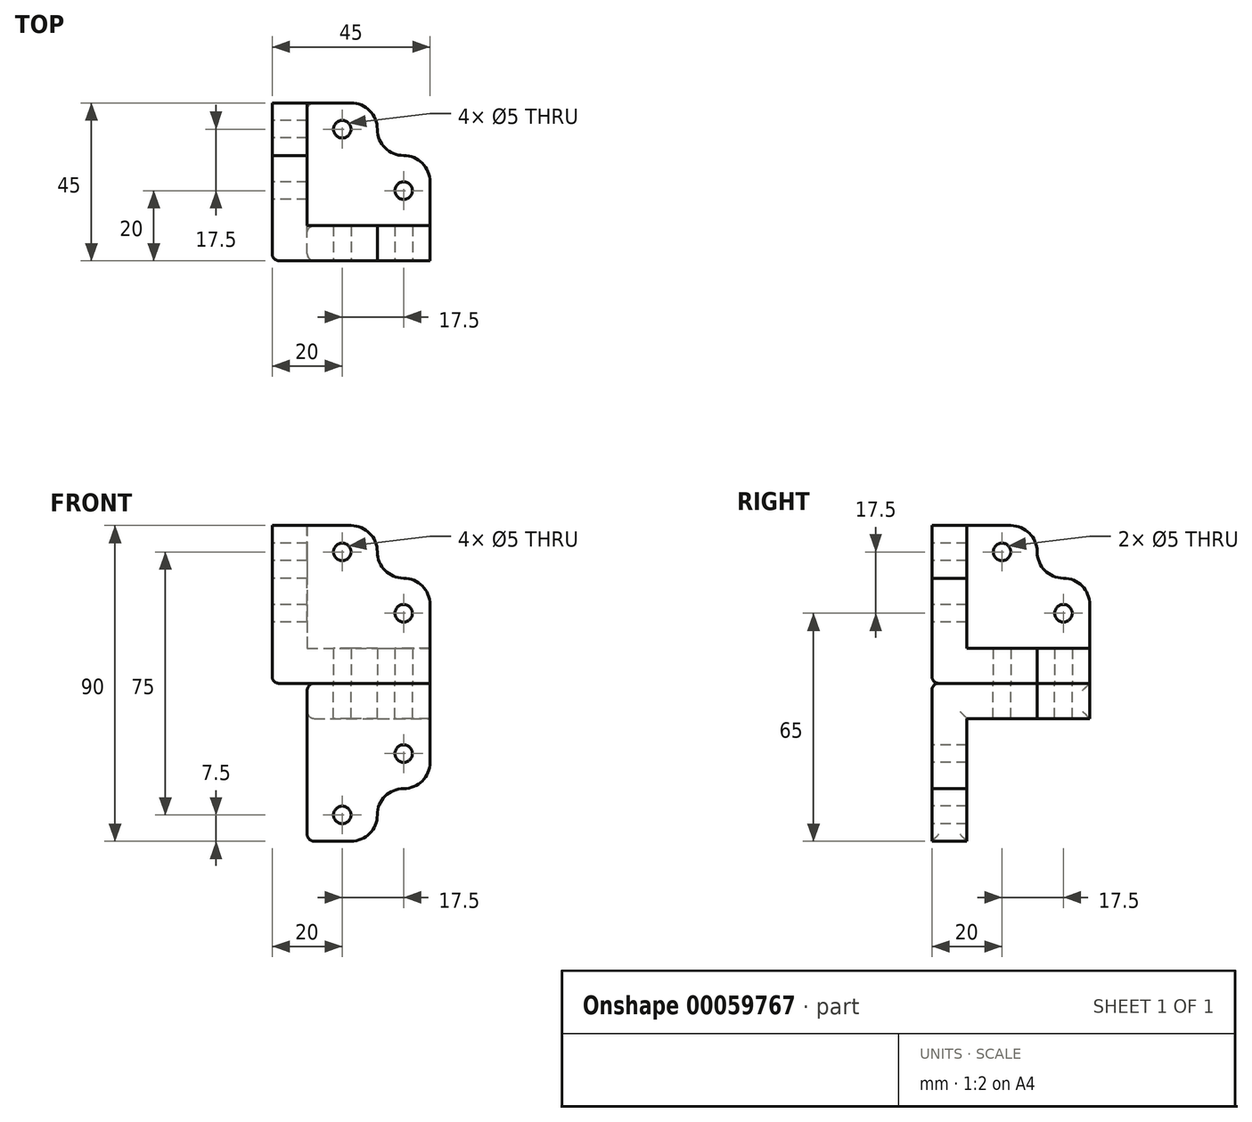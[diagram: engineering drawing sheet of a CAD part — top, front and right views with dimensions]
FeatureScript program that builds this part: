
annotation { "Feature Type Name" : "Feature", "Feature Type Description" : "" }
export const myFeature = defineFeature(function(context is Context, id is Id, definition is map)
    precondition{}
    {
        {
            var Q0;
            Q0=qCreatedBy(makeId("Top.planeOp"),FACE);
            var sketch = newSketch(context, id + "F0", { "sketchPlane" : qUnion([Q0])});
            skLineSegment(sketch, "E0", {"start": v(10, 45) * mm, "end": v(10, 10) * mm});
            skLineSegment(sketch, "E1", {"start": v(10, 10) * mm, "end": v(45, 10) * mm});
            skLineSegment(sketch, "E2", {"start": v(45, 10) * mm, "end": v(45, 30) * mm});
            skLineSegment(sketch, "E3", {"start": v(45, 30) * mm, "end": v(30, 30) * mm});
            skLineSegment(sketch, "E4", {"start": v(30, 30) * mm, "end": v(30, 45) * mm});
            skLineSegment(sketch, "E5", {"start": v(30, 45) * mm, "end": v(10, 45) * mm});
            skLineSegment(sketch, "E6", {"start": v(45, 10) * mm, "end": v(45, 0) * mm});
            skLineSegment(sketch, "E7", {"start": v(45, 0) * mm, "end": v(0, 0) * mm});
            skLineSegment(sketch, "E8", {"start": v(0, 0) * mm, "end": v(0, 45) * mm});
            skLineSegment(sketch, "E9", {"start": v(0, 45) * mm, "end": v(10, 45) * mm});
            skCircle(sketch, "E10", {"center": v(20, 37.5) * mm, "radius": 2.5 * mm});
            skPoint(sketch, "E10.centerSnap0", {"position": v(30, 37.5) * mm});
            skPoint(sketch, "E10.centerSnap1", {"position": v(20, 45) * mm});
            skCircle(sketch, "E11", {"center": v(37.5, 20) * mm, "radius": 2.5 * mm});
            skPoint(sketch, "E11.centerSnap0", {"position": v(45, 20) * mm});
            skPoint(sketch, "E11.centerSnap1", {"position": v(37.5, 30) * mm});
            skPoint(sketch, "E12.0", {"position": v(0, 0) * mm});
            skSolve(sketch);
        }
        {
            var Q0;
            Q0=makeQuery(id+"F0.imprint","IMPRINT",FACE,{"disambiguationData":[TD([[makeQuery(id+"F0.imprint","IMPRINT",EDGE,{"derivedFrom":sQuery(id+"F0.wireOp",EDGE,"E0")}),-1.0]])]});
            var Q1;
            Q1=makeQuery(id+"F0.imprint","IMPRINT",FACE,{"disambiguationData":[TD([[makeQuery(id+"F0.imprint","IMPRINT",EDGE,{"derivedFrom":sQuery(id+"F0.wireOp",EDGE,"E0")}),1.0]])]});
            extrude(context, id + "F1", {"entities" : qUnion([Q0, Q1]), "depth" : 10 * mm});
        }
        {
            var Q0;
            Q0=qCreatedBy(makeId("Right.planeOp"),FACE);
            var sketch = newSketch(context, id + "F2", { "sketchPlane" : qUnion([Q0])});
            skLineSegment(sketch, "E13", {"start": v(10, 45) * mm, "end": v(10, 10) * mm});
            skLineSegment(sketch, "E14", {"start": v(10, 10) * mm, "end": v(45, 10) * mm});
            skLineSegment(sketch, "E15", {"start": v(45, 10) * mm, "end": v(45, 30) * mm});
            skLineSegment(sketch, "E16", {"start": v(45, 30) * mm, "end": v(30, 30) * mm});
            skLineSegment(sketch, "E17", {"start": v(30, 30) * mm, "end": v(30, 45) * mm});
            skLineSegment(sketch, "E18", {"start": v(30, 45) * mm, "end": v(10, 45) * mm});
            skLineSegment(sketch, "E19", {"start": v(45, 10) * mm, "end": v(45, 0) * mm});
            skLineSegment(sketch, "E20", {"start": v(45, 0) * mm, "end": v(0, 0) * mm});
            skLineSegment(sketch, "E21", {"start": v(0, 0) * mm, "end": v(0, 45) * mm});
            skLineSegment(sketch, "E22", {"start": v(0, 45) * mm, "end": v(10, 45) * mm});
            skCircle(sketch, "E23", {"center": v(20, 37.5) * mm, "radius": 2.5 * mm});
            skPoint(sketch, "E23.centerSnap0", {"position": v(30, 37.5) * mm});
            skPoint(sketch, "E23.centerSnap1", {"position": v(20, 45) * mm});
            skCircle(sketch, "E24", {"center": v(37.5, 20) * mm, "radius": 2.5 * mm});
            skPoint(sketch, "E24.centerSnap0", {"position": v(45, 20) * mm});
            skPoint(sketch, "E24.centerSnap1", {"position": v(37.5, 30) * mm});
            skPoint(sketch, "E25", {"position": v(0, 0) * mm});
            skSolve(sketch);
        }
        {
            var Q0;
            Q0=makeQuery(id+"F2.imprint","IMPRINT",FACE,{"disambiguationData":[TD([[makeQuery(id+"F2.imprint","IMPRINT",EDGE,{"derivedFrom":sQuery(id+"F2.wireOp",EDGE,"2a13ad23-5e3c-4e8f-b476-5bc90f6551fb")}),1.0]])]});
            var Q1;
            Q1=makeQuery(id+"F2.imprint","IMPRINT",FACE,{"disambiguationData":[TD([[makeQuery(id+"F2.imprint","IMPRINT",EDGE,{"derivedFrom":sQuery(id+"F2.wireOp",EDGE,"2a13ad23-5e3c-4e8f-b476-5bc90f6551fb")}),-1.0]])]});
            var Q2;
            Q2=makeQuery(id+"F2.imprint","IMPRINT",FACE,{"disambiguationData":[TD([[makeQuery(id+"F2.imprint","IMPRINT",EDGE,{"derivedFrom":sQuery(id+"F2.wireOp",EDGE,"E13")}),-1.0]])]});
            var Q3;
            Q3=makeQuery(id+"F2.imprint","IMPRINT",FACE,{"disambiguationData":[TD([[makeQuery(id+"F2.imprint","IMPRINT",EDGE,{"derivedFrom":sQuery(id+"F2.wireOp",EDGE,"E13")}),1.0]])]});
            extrude(context, id + "F3", {"entities" : qUnion([Q0, Q1, Q2, Q3]), "operationType" : NewBodyOperationType.ADD, "depth" : 10 * mm});
        }
        {
            var Q0;
            Q0=qCreatedBy(makeId("Front.planeOp"),FACE);
            var sketch = newSketch(context, id + "F4", { "sketchPlane" : qUnion([Q0])});
            skPoint(sketch, "E26", {"position": v(0, 0) * mm});
            skLineSegment(sketch, "E27", {"start": v(10, 45) * mm, "end": v(10, 10) * mm});
            skLineSegment(sketch, "E28", {"start": v(10, 10) * mm, "end": v(45, 10) * mm});
            skLineSegment(sketch, "E29", {"start": v(45, 10) * mm, "end": v(45, 30) * mm});
            skLineSegment(sketch, "E30", {"start": v(45, 30) * mm, "end": v(30, 30) * mm});
            skLineSegment(sketch, "E31", {"start": v(30, 30) * mm, "end": v(30, 45) * mm});
            skLineSegment(sketch, "E32", {"start": v(30, 45) * mm, "end": v(10, 45) * mm});
            skLineSegment(sketch, "E33", {"start": v(45, 10) * mm, "end": v(45, 0) * mm});
            skLineSegment(sketch, "E34", {"start": v(45, 0) * mm, "end": v(0, 0) * mm});
            skLineSegment(sketch, "E35", {"start": v(0, 0) * mm, "end": v(0, 45) * mm});
            skLineSegment(sketch, "E36", {"start": v(0, 45) * mm, "end": v(10, 45) * mm});
            skCircle(sketch, "E37", {"center": v(20, 37.5) * mm, "radius": 2.5 * mm});
            skPoint(sketch, "E37.centerSnap0", {"position": v(30, 37.5) * mm});
            skPoint(sketch, "E37.centerSnap1", {"position": v(20, 45) * mm});
            skCircle(sketch, "E38", {"center": v(37.5, 20) * mm, "radius": 2.5 * mm});
            skPoint(sketch, "E38.centerSnap0", {"position": v(45, 20) * mm});
            skPoint(sketch, "E38.centerSnap1", {"position": v(37.5, 30) * mm});
            skSolve(sketch);
        }
        {
            var Q0;
            Q0=makeQuery(id+"F4.imprint","IMPRINT",FACE,{"disambiguationData":[TD([[makeQuery(id+"F4.imprint","IMPRINT",EDGE,{"derivedFrom":sQuery(id+"F4.wireOp",EDGE,"64c80488-47ea-4c83-bcab-fc076bb4a540")}),-1.0]])]});
            var Q1;
            Q1=makeQuery(id+"F4.imprint","IMPRINT",FACE,{"disambiguationData":[TD([[makeQuery(id+"F4.imprint","IMPRINT",EDGE,{"derivedFrom":sQuery(id+"F4.wireOp",EDGE,"64c80488-47ea-4c83-bcab-fc076bb4a540")}),1.0]])]});
            var Q2;
            Q2=makeQuery(id+"F4.imprint","IMPRINT",FACE,{"disambiguationData":[TD([[makeQuery(id+"F4.imprint","IMPRINT",EDGE,{"derivedFrom":sQuery(id+"F4.wireOp",EDGE,"E27")}),-1.0]])]});
            var Q3;
            Q3=makeQuery(id+"F4.imprint","IMPRINT",FACE,{"disambiguationData":[TD([[makeQuery(id+"F4.imprint","IMPRINT",EDGE,{"derivedFrom":sQuery(id+"F4.wireOp",EDGE,"E27")}),1.0]])]});
            extrude(context, id + "F5", {"entities" : qUnion([Q0, Q1, Q2, Q3]), "operationType" : NewBodyOperationType.ADD, "oppositeDirection" : true, "depth" : 10 * mm});
        }
        {
            var Q0;
            Q0=makeQuery(id+"F1.opExtrude","CAP_EDGE",EDGE,{"disambiguationData":[OSD([sQuery(id+"F0.wireOp",EDGE,"E7")])],"isStart":true});
            var Q1;
            Q1=makeQuery(id+"F3.boolean.opBoolean","MERGE",EDGE,{"derivedFrom":[makeQuery(id+"F1.opExtrude","SWEPT_EDGE",EDGE,{"disambiguationData":[OSD([sQuery(id+"F0.wireOp",EDGE,"E7"),sQuery(id+"F0.wireOp",EDGE,"E8")])]}),makeQuery(id+"F3.opExtrude","CAP_EDGE",EDGE,{"disambiguationData":[OSD([sQuery(id+"F2.wireOp",EDGE,"E21")])],"isStart":true})]});
            var Q2;
            Q2=makeQuery(id+"F1.opExtrude","CAP_EDGE",EDGE,{"disambiguationData":[OSD([sQuery(id+"F0.wireOp",EDGE,"E8")])],"isStart":true});
            fillet(context, id + "F6", {"entities" : qUnion([Q0, Q1, Q2]), "radius" : 2 * mm, "tangentPropagation" : true, "allowEdgeOverflow" : false});
        }
        {
            var Q0;
            Q0=makeQuery(id+"F5.opExtrude","SWEPT_EDGE",EDGE,{"disambiguationData":[OSD([sQuery(id+"F4.wireOp",EDGE,"E29"),sQuery(id+"F4.wireOp",EDGE,"E30")])]});
            var Q1;
            Q1=makeQuery(id+"F5.opExtrude","SWEPT_EDGE",EDGE,{"disambiguationData":[OSD([sQuery(id+"F4.wireOp",EDGE,"E31"),sQuery(id+"F4.wireOp",EDGE,"E32")])]});
            var Q2;
            Q2=makeQuery(id+"F3.opExtrude","SWEPT_EDGE",EDGE,{"disambiguationData":[OSD([sQuery(id+"F2.wireOp",EDGE,"E17"),sQuery(id+"F2.wireOp",EDGE,"E18")])]});
            var Q3;
            Q3=makeQuery(id+"F3.opExtrude","SWEPT_EDGE",EDGE,{"disambiguationData":[OSD([sQuery(id+"F2.wireOp",EDGE,"E15"),sQuery(id+"F2.wireOp",EDGE,"E16")])]});
            var Q4;
            Q4=makeQuery(id+"F1.opExtrude","SWEPT_EDGE",EDGE,{"disambiguationData":[OSD([sQuery(id+"F0.wireOp",EDGE,"E4"),sQuery(id+"F0.wireOp",EDGE,"E5")])]});
            var Q5;
            Q5=makeQuery(id+"F1.opExtrude","SWEPT_EDGE",EDGE,{"disambiguationData":[OSD([sQuery(id+"F0.wireOp",EDGE,"E2"),sQuery(id+"F0.wireOp",EDGE,"E3")])]});
            fillet(context, id + "F7", {"entities" : qUnion([Q0, Q1, Q2, Q3, Q4, Q5]), "radius" : 7.5 * mm, "tangentPropagation" : true, "allowEdgeOverflow" : false});
        }
        {
            var Q0;
            Q0=makeQuery(id+"F5.opExtrude","SWEPT_EDGE",EDGE,{"disambiguationData":[OSD([sQuery(id+"F4.wireOp",EDGE,"E30"),sQuery(id+"F4.wireOp",EDGE,"E31")])]});
            var Q1;
            Q1=makeQuery(id+"F1.opExtrude","SWEPT_EDGE",EDGE,{"disambiguationData":[OSD([sQuery(id+"F0.wireOp",EDGE,"E3"),sQuery(id+"F0.wireOp",EDGE,"E4")])]});
            var Q2;
            Q2=makeQuery(id+"F3.opExtrude","SWEPT_EDGE",EDGE,{"disambiguationData":[OSD([sQuery(id+"F2.wireOp",EDGE,"E16"),sQuery(id+"F2.wireOp",EDGE,"E17")])]});
            fillet(context, id + "F8", {"entities" : qUnion([Q0, Q1, Q2]), "radius" : 7.5 * mm, "tangentPropagation" : true, "allowEdgeOverflow" : false});
        }
        {
            var Q0;
            Q0=makeQuery(id+"F1.opExtrude","SWEPT_BODY",BODY,{"disambiguationData":[OSD([sQuery(id+"F0.wireOp",EDGE,"E2"),sQuery(id+"F0.wireOp",EDGE,"E3"),sQuery(id+"F0.wireOp",EDGE,"E4"),sQuery(id+"F0.wireOp",EDGE,"E5"),sQuery(id+"F0.wireOp",EDGE,"E6"),sQuery(id+"F0.wireOp",EDGE,"E7"),sQuery(id+"F0.wireOp",EDGE,"E8"),sQuery(id+"F0.wireOp",EDGE,"E9"),sQuery(id+"F0.wireOp",EDGE,"E10"),sQuery(id+"F0.wireOp",EDGE,"E11")])]});
            var Q1;
            Q1 = qSketchRegion(id + "F0", true);
            mirror(context, id + "F9", {"entities" : qUnion([Q0]), "mirrorPlane" : qUnion([Q1])});
        }
        {
            var Q0;
            Q0=makeQuery(id+"F9.opPattern","COPY",FACE,{"derivedFrom":makeQuery(id+"F3.boolean.opBoolean","MERGE",FACE,{"derivedFrom":[makeQuery(id+"F1.opExtrude","SWEPT_FACE",FACE,{"disambiguationData":[OSD([sQuery(id+"F0.wireOp",EDGE,"E8")])]}),makeQuery(id+"F3.opExtrude","CAP_FACE",FACE,{"disambiguationData":[OSD([sQuery(id+"F2.wireOp",EDGE,"E15"),sQuery(id+"F2.wireOp",EDGE,"E16"),sQuery(id+"F2.wireOp",EDGE,"E17"),sQuery(id+"F2.wireOp",EDGE,"E18"),sQuery(id+"F2.wireOp",EDGE,"E19"),sQuery(id+"F2.wireOp",EDGE,"E20"),sQuery(id+"F2.wireOp",EDGE,"E21"),sQuery(id+"F2.wireOp",EDGE,"E22"),sQuery(id+"F2.wireOp",EDGE,"E23"),sQuery(id+"F2.wireOp",EDGE,"E24")])],"isStart":true})]}),"instanceName":"1"});
            var sketch = newSketch(context, id + "F10", { "sketchPlane" : qUnion([Q0])});
            skLineSegment(sketch, "E39.0", {"start": v(-45, -22.5) * mm, "end": v(-45, -2) * mm});
            skArc(sketch, "E40.0", {"start": v(-37.5, -30) * mm, "mid": v(-42.8, -27.8) * mm, "end": v(-45, -22.5) * mm});
            skArc(sketch, "E41.0", {"start": v(-30, -37.5) * mm, "mid": v(-32.2, -32.2) * mm, "end": v(-37.5, -30) * mm});
            skArc(sketch, "E42.0", {"start": v(-22.5, -45) * mm, "mid": v(-27.8, -42.8) * mm, "end": v(-30, -37.5) * mm});
            skLineSegment(sketch, "E43.0", {"start": v(-2, -45) * mm, "end": v(-22.5, -45) * mm});
            skLineSegment(sketch, "E44.0.0", {"start": v(0, -30) * mm, "end": v(0, -22.5) * mm});
            skLineSegment(sketch, "E44.0.1", {"start": v(0, -22.5) * mm, "end": v(0, -2) * mm});
            skLineSegment(sketch, "E44.0.3", {"start": v(0, -2) * mm, "end": v(0, -45) * mm});
            skLineSegment(sketch, "E44.0.5", {"start": v(0, -45) * mm, "end": v(0, -37.5) * mm});
            skLineSegment(sketch, "E44.0.6", {"start": v(0, -30) * mm, "end": v(0, -37.5) * mm});
            skLineSegment(sketch, "E45.0", {"start": v(-2, -45) * mm, "end": v(0, -45) * mm});
            skLineSegment(sketch, "E46.0", {"start": v(0, 0) * mm, "end": v(-45, 0) * mm});
            skArc(sketch, "E47.0", {"start": v(-2, 0) * mm, "mid": v(-0.59, -0.59) * mm, "end": v(0, -2) * mm});
            skLineSegment(sketch, "E48.0", {"start": v(-45, 0) * mm, "end": v(-45, -2) * mm});
            skSolve(sketch);
        }
        {
            var Q0;
            Q0=makeQuery(id+"F10.imprint","IMPRINT",FACE,{"disambiguationData":[TD([[makeQuery(id+"F10.imprint","IMPRINT",EDGE,{"derivedFrom":sQuery(id+"F10.wireOp",EDGE,"E39.0")}),-1.0]])]});
            var Q1;
            Q1=makeQuery(id+"F10.imprint","IMPRINT",FACE,{"disambiguationData":[TD([[makeQuery(id+"F10.imprint","IMPRINT",EDGE,{"derivedFrom":sQuery(id+"F10.wireOp",EDGE,"E44.0.3")}),-1.0]])]});
            var Q2;
            Q2=makeQuery(id+"F9.opPattern","COPY",FACE,{"derivedFrom":makeQuery(id+"F3.opExtrude","CAP_FACE",FACE,{"disambiguationData":[OSD([sQuery(id+"F2.wireOp",EDGE,"E15"),sQuery(id+"F2.wireOp",EDGE,"E16"),sQuery(id+"F2.wireOp",EDGE,"E17"),sQuery(id+"F2.wireOp",EDGE,"E18"),sQuery(id+"F2.wireOp",EDGE,"E19"),sQuery(id+"F2.wireOp",EDGE,"E20"),sQuery(id+"F2.wireOp",EDGE,"E21"),sQuery(id+"F2.wireOp",EDGE,"E22"),sQuery(id+"F2.wireOp",EDGE,"E23"),sQuery(id+"F2.wireOp",EDGE,"E24")])],"isStart":false}),"instanceName":"1"});
            extrude(context, id + "F11", {"entities" : qUnion([Q0, Q1]), "operationType" : NewBodyOperationType.REMOVE, "endBound" : BoundingType.UP_TO_SURFACE, "oppositeDirection" : true, "depth" : 25 * mm, "endBoundEntityFace" : qUnion([Q2]), "offsetDistance" : 25 * mm});
        }
        {
            var Q0;
            Q0=makeQuery(id+"F11.boolean.opBoolean","COPY",FACE,{"derivedFrom":makeQuery(id+"F11.opExtrude","CAP_FACE",FACE,{"disambiguationData":[OSD([sQuery(id+"F2.wireOp",EDGE,"E23"),sQuery(id+"F2.wireOp",EDGE,"E24"),sQuery(id+"F10.wireOp",EDGE,"E39.0"),sQuery(id+"F10.wireOp",EDGE,"E40.0"),sQuery(id+"F10.wireOp",EDGE,"E41.0"),sQuery(id+"F10.wireOp",EDGE,"E42.0"),sQuery(id+"F10.wireOp",EDGE,"E43.0"),sQuery(id+"F10.wireOp",EDGE,"E44.0.3"),sQuery(id+"F10.wireOp",EDGE,"E44.0.5"),sQuery(id+"F10.wireOp",EDGE,"E44.0.6"),sQuery(id+"F10.wireOp",EDGE,"E45.0"),sQuery(id+"F10.wireOp",EDGE,"E46.0"),sQuery(id+"F10.wireOp",EDGE,"E47.0"),sQuery(id+"F10.wireOp",EDGE,"E48.0")])],"isStart":false})});
            fillet(context, id + "F12", {"entities" : qUnion([Q0]), "radius" : 2 * mm, "tangentPropagation" : true, "allowEdgeOverflow" : false});
        }
    });
